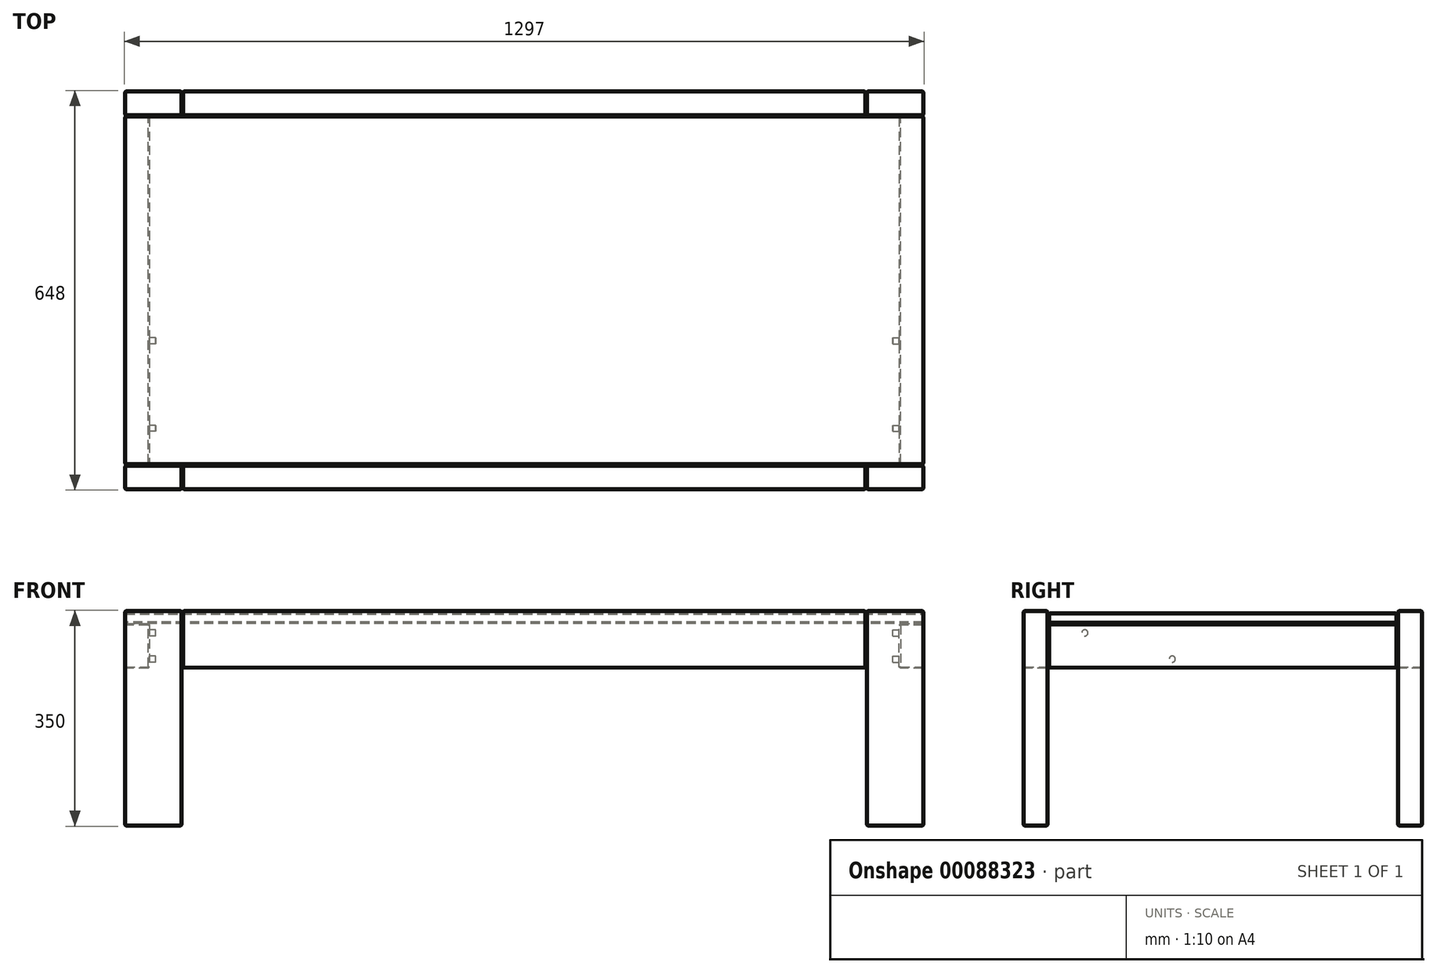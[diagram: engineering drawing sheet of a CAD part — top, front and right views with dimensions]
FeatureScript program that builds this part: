
annotation { "Feature Type Name" : "Feature", "Feature Type Description" : "" }
export const myFeature = defineFeature(function(context is Context, id is Id, definition is map)
    precondition{}
    {
        {
            var Q0;
            Q0=qCreatedBy(makeId("Top.planeOp"),FACE);
            var sketch = newSketch(context, id + "F0", { "sketchPlane" : qUnion([Q0])});
            skLineSegment(sketch, "E0.bottom", {"start": v(-648.5, 324) * mm, "end": v(648.5, 324) * mm, "construction": true});
            skLineSegment(sketch, "E0.top", {"start": v(-648.5, -324) * mm, "end": v(648.5, -324) * mm, "construction": true});
            skLineSegment(sketch, "E0.left", {"start": v(-648.5, 324) * mm, "end": v(-648.5, -324) * mm, "construction": true});
            skLineSegment(sketch, "E0.right", {"start": v(648.5, 324) * mm, "end": v(648.5, -324) * mm, "construction": true});
            skLineSegment(sketch, "E1", {"start": v(-648.5, -324) * mm, "end": v(648.5, 324) * mm, "construction": true});
            skLineSegment(sketch, "E2.bottom", {"start": v(-648.5, 324) * mm, "end": v(-554.5, 324) * mm});
            skLineSegment(sketch, "E2.top", {"start": v(-648.5, 283) * mm, "end": v(-554.5, 283) * mm});
            skLineSegment(sketch, "E2.left", {"start": v(-648.5, 324) * mm, "end": v(-648.5, 283) * mm});
            skLineSegment(sketch, "E2.right", {"start": v(-554.5, 324) * mm, "end": v(-554.5, 283) * mm});
            skLineSegment(sketch, "E3.bottom", {"start": v(-648.5, -324) * mm, "end": v(-554.5, -324) * mm});
            skLineSegment(sketch, "E3.top", {"start": v(-648.5, -283) * mm, "end": v(-554.5, -283) * mm});
            skLineSegment(sketch, "E3.left", {"start": v(-648.5, -324) * mm, "end": v(-648.5, -283) * mm});
            skLineSegment(sketch, "E3.right", {"start": v(-554.5, -324) * mm, "end": v(-554.5, -283) * mm});
            skLineSegment(sketch, "E4.bottom", {"start": v(648.5, 324) * mm, "end": v(554.5, 324) * mm});
            skLineSegment(sketch, "E4.top", {"start": v(648.5, 283) * mm, "end": v(554.5, 283) * mm});
            skLineSegment(sketch, "E4.left", {"start": v(648.5, 324) * mm, "end": v(648.5, 283) * mm});
            skLineSegment(sketch, "E4.right", {"start": v(554.5, 324) * mm, "end": v(554.5, 283) * mm});
            skLineSegment(sketch, "E5.bottom", {"start": v(648.5, -324) * mm, "end": v(554.5, -324) * mm});
            skLineSegment(sketch, "E5.top", {"start": v(648.5, -283) * mm, "end": v(554.5, -283) * mm});
            skLineSegment(sketch, "E5.left", {"start": v(648.5, -324) * mm, "end": v(648.5, -283) * mm});
            skLineSegment(sketch, "E5.right", {"start": v(554.5, -324) * mm, "end": v(554.5, -283) * mm});
            skSolve(sketch);
        }
        {
            var Q0;
            Q0 = qSketchRegion(id + "F0", true);
            extrude(context, id + "F1", {"entities" : qUnion([Q0]), "depth" : 350 * mm});
        }
        {
            var Q0;
            Q0=makeQuery(id+"F1.opExtrude","SWEPT_FACE",FACE,{"disambiguationData":[OSD([sQuery(id+"F0.wireOp",EDGE,"E3.right")])]});
            var sketch = newSketch(context, id + "F2", { "sketchPlane" : qUnion([Q0])});
            skLineSegment(sketch, "E6.bottom", {"start": v(-324, 350) * mm, "end": v(-283, 350) * mm});
            skLineSegment(sketch, "E6.top", {"start": v(-324, 256) * mm, "end": v(-283, 256) * mm});
            skLineSegment(sketch, "E6.left", {"start": v(-324, 350) * mm, "end": v(-324, 256) * mm});
            skLineSegment(sketch, "E6.right", {"start": v(-283, 350) * mm, "end": v(-283, 256) * mm});
            skLineSegment(sketch, "E7.bottom", {"start": v(283, 350) * mm, "end": v(324, 350) * mm});
            skLineSegment(sketch, "E7.top", {"start": v(283, 256) * mm, "end": v(324, 256) * mm});
            skLineSegment(sketch, "E7.left", {"start": v(283, 350) * mm, "end": v(283, 256) * mm});
            skLineSegment(sketch, "E7.right", {"start": v(324, 350) * mm, "end": v(324, 256) * mm});
            skSolve(sketch);
        }
        {
            var Q0;
            Q0 = qSketchRegion(id + "F2", true);
            var Q1;
            Q1=makeQuery(id+"F1.opExtrude","SWEPT_FACE",FACE,{"disambiguationData":[OSD([sQuery(id+"F0.wireOp",EDGE,"E5.right")])]});
            extrude(context, id + "F3", {"entities" : qUnion([Q0]), "endBound" : BoundingType.UP_TO_SURFACE, "endBoundEntityFace" : qUnion([Q1]), "depth" : 25 * mm});
        }
        {
            var Q0;
            Q0=makeQuery(id+"F3.opExtrude","SWEPT_FACE",FACE,{"disambiguationData":[OSD([sQuery(id+"F2.wireOp",EDGE,"E7.bottom")])]});
            cPlane(context, id + "F4", {"entities" : qUnion([Q0]), "cplaneType" : CPlaneType.OFFSET, "offset" : 3.5 * mm, "oppositeDirection" : true, "width" : 150 * mm, "height" : 150 * mm});
        }
        {
            var Q0;
            Q0=qCreatedBy(id+"F4.planeOp",FACE);
            var sketch = newSketch(context, id + "F5", { "sketchPlane" : qUnion([Q0])});
            skLineSegment(sketch, "E8.bottom", {"start": v(-648.5, 283) * mm, "end": v(648.5, 283) * mm});
            skLineSegment(sketch, "E8.top", {"start": v(-648.5, -283) * mm, "end": v(648.5, -283) * mm});
            skLineSegment(sketch, "E8.left", {"start": v(-648.5, 283) * mm, "end": v(-648.5, -283) * mm});
            skLineSegment(sketch, "E8.right", {"start": v(648.5, 283) * mm, "end": v(648.5, -283) * mm});
            skSolve(sketch);
        }
        {
            var Q0;
            Q0 = qSketchRegion(id + "F5", true);
            extrude(context, id + "F6", {"entities" : qUnion([Q0]), "oppositeDirection" : true, "depth" : 18 * mm});
        }
        {
            var Q0;
            Q0=makeQuery(id+"F1.opExtrude","SWEPT_FACE",FACE,{"disambiguationData":[OSD([sQuery(id+"F0.wireOp",EDGE,"E2.top")])]});
            var sketch = newSketch(context, id + "F7", { "sketchPlane" : qUnion([Q0])});
            skLineSegment(sketch, "E9", {"start": v(-648.5, 350) * mm, "end": v(-648.5, 256) * mm, "construction": true});
            skLineSegment(sketch, "E10.bottom", {"start": v(-648.5, 256) * mm, "end": v(-607.5, 256) * mm});
            skLineSegment(sketch, "E10.top", {"start": v(-648.5, 328.5) * mm, "end": v(-607.5, 328.5) * mm});
            skLineSegment(sketch, "E10.left", {"start": v(-648.5, 256) * mm, "end": v(-648.5, 328.5) * mm});
            skLineSegment(sketch, "E10.right", {"start": v(-607.5, 256) * mm, "end": v(-607.5, 328.5) * mm});
            skLineSegment(sketch, "E11", {"start": v(-607.5, 328.5) * mm, "end": v(-607.5, 350) * mm, "construction": true});
            skLineSegment(sketch, "E12.bottom", {"start": v(648.5, 328.5) * mm, "end": v(607.5, 328.5) * mm});
            skLineSegment(sketch, "E12.top", {"start": v(648.5, 256) * mm, "end": v(607.5, 256) * mm});
            skLineSegment(sketch, "E12.left", {"start": v(648.5, 328.5) * mm, "end": v(648.5, 256) * mm});
            skLineSegment(sketch, "E12.right", {"start": v(607.5, 328.5) * mm, "end": v(607.5, 256) * mm});
            skSolve(sketch);
        }
        {
            var Q0;
            Q0 = qSketchRegion(id + "F7", true);
            var Q1;
            Q1=makeQuery(id+"F1.opExtrude","SWEPT_FACE",FACE,{"disambiguationData":[OSD([sQuery(id+"F0.wireOp",EDGE,"E3.top")])]});
            extrude(context, id + "F8", {"entities" : qUnion([Q0]), "endBound" : BoundingType.UP_TO_SURFACE, "endBoundEntityFace" : qUnion([Q1]), "depth" : 25 * mm});
        }
        {
            var Q0;
            Q0=makeQuery(id+"F8.opExtrude","SWEPT_FACE",FACE,{"disambiguationData":[OSD([sQuery(id+"F7.wireOp",EDGE,"E10.right")])]});
            var sketch = newSketch(context, id + "F9", { "sketchPlane" : qUnion([Q0])});
            skPoint(sketch, "E13", {"position": v(-82, 271) * mm});
            skPoint(sketch, "E14", {"position": v(-223.7, 313.5) * mm});
            skLineSegment(sketch, "E15", {"start": v(-223.7, 313.5) * mm, "end": v(-230.84, 300.3) * mm, "construction": true});
            skLineSegment(sketch, "E16", {"start": v(-230.84, 300.3) * mm, "end": v(-283, 328.5) * mm, "construction": true});
            skLineSegment(sketch, "E17", {"start": v(-223.7, 313.5) * mm, "end": v(-531.6, 479.94) * mm, "construction": true});
            skLineSegment(sketch, "E18", {"start": v(-389.9, 437.44) * mm, "end": v(-82, 271) * mm, "construction": true});
            skLineSegment(sketch, "E19", {"start": v(-389.9, 437.44) * mm, "end": v(-531.6, 479.94) * mm, "construction": true});
            skLineSegment(sketch, "E20", {"start": v(-82, 271) * mm, "end": v(268, 271) * mm, "construction": true});
            skCircle(sketch, "E21", {"center": v(-223.7, 313.5) * mm, "radius": 5 * mm});
            skCircle(sketch, "E22", {"center": v(-82, 271) * mm, "radius": 5 * mm});
            skSolve(sketch);
        }
        {
            var Q0;
            Q0=makeQuery(id+"F3.opExtrude","CAP_EDGE",EDGE,{"disambiguationData":[OSD([sQuery(id+"F2.wireOp",EDGE,"E7.right")])],"isStart":true});
            var Q1;
            Q1=makeQuery(id+"F3.opExtrude","CAP_EDGE",EDGE,{"disambiguationData":[OSD([sQuery(id+"F2.wireOp",EDGE,"E7.left")])],"isStart":false});
            var Q2;
            Q2=makeQuery(id+"F3.opExtrude","CAP_EDGE",EDGE,{"disambiguationData":[OSD([sQuery(id+"F2.wireOp",EDGE,"E7.left")])],"isStart":true});
            var Q3;
            Q3=makeQuery(id+"F3.opExtrude","CAP_EDGE",EDGE,{"disambiguationData":[OSD([sQuery(id+"F2.wireOp",EDGE,"E7.top")])],"isStart":false});
            var Q4;
            Q4=makeQuery(id+"F1.opExtrude","CAP_EDGE",EDGE,{"disambiguationData":[OSD([sQuery(id+"F0.wireOp",EDGE,"E2.right")])],"isStart":false});
            var Q5;
            Q5=makeQuery(id+"F1.opExtrude","CAP_EDGE",EDGE,{"disambiguationData":[OSD([sQuery(id+"F0.wireOp",EDGE,"E3.right")])],"isStart":false});
            var Q6;
            Q6=makeQuery(id+"F1.opExtrude","CAP_EDGE",EDGE,{"disambiguationData":[OSD([sQuery(id+"F0.wireOp",EDGE,"E4.right")])],"isStart":false});
            var Q7;
            Q7=makeQuery(id+"F1.opExtrude","CAP_EDGE",EDGE,{"disambiguationData":[OSD([sQuery(id+"F0.wireOp",EDGE,"E5.right")])],"isStart":false});
            var Q8;
            Q8=makeQuery(id+"F1.opExtrude","CAP_EDGE",EDGE,{"disambiguationData":[OSD([sQuery(id+"F0.wireOp",EDGE,"E5.bottom")])],"isStart":true});
            var Q9;
            Q9=makeQuery(id+"F1.opExtrude","CAP_EDGE",EDGE,{"disambiguationData":[OSD([sQuery(id+"F0.wireOp",EDGE,"E5.top")])],"isStart":false});
            var Q10;
            Q10=makeQuery(id+"F1.opExtrude","CAP_EDGE",EDGE,{"disambiguationData":[OSD([sQuery(id+"F0.wireOp",EDGE,"E5.top")])],"isStart":true});
            var Q11;
            Q11=makeQuery(id+"F3.opExtrude","CAP_EDGE",EDGE,{"disambiguationData":[OSD([sQuery(id+"F2.wireOp",EDGE,"E7.right")])],"isStart":false});
            var Q12;
            Q12=makeQuery(id+"F3.opExtrude","CAP_EDGE",EDGE,{"disambiguationData":[OSD([sQuery(id+"F2.wireOp",EDGE,"E6.bottom")])],"isStart":false});
            var Q13;
            Q13=makeQuery(id+"F3.opExtrude","CAP_EDGE",EDGE,{"disambiguationData":[OSD([sQuery(id+"F2.wireOp",EDGE,"E7.bottom")])],"isStart":true});
            var Q14;
            Q14=makeQuery(id+"F3.opExtrude","CAP_EDGE",EDGE,{"disambiguationData":[OSD([sQuery(id+"F2.wireOp",EDGE,"E7.bottom")])],"isStart":false});
            var Q15;
            Q15=makeQuery(id+"F3.opExtrude","SWEPT_EDGE",EDGE,{"disambiguationData":[OSD([sQuery(id+"F2.wireOp",EDGE,"E7.bottom"),sQuery(id+"F2.wireOp",EDGE,"E7.right")])]});
            var Q16;
            Q16=makeQuery(id+"F1.opExtrude","SWEPT_EDGE",EDGE,{"disambiguationData":[OSD([sQuery(id+"F0.wireOp",EDGE,"E2.top"),sQuery(id+"F0.wireOp",EDGE,"E2.right")])]});
            var Q17;
            Q17=makeQuery(id+"F1.opExtrude","SWEPT_EDGE",EDGE,{"disambiguationData":[OSD([sQuery(id+"F0.wireOp",EDGE,"E2.bottom"),sQuery(id+"F0.wireOp",EDGE,"E2.right")])]});
            var Q18;
            Q18=makeQuery(id+"F1.opExtrude","SWEPT_EDGE",EDGE,{"disambiguationData":[OSD([sQuery(id+"F0.wireOp",EDGE,"E2.top"),sQuery(id+"F0.wireOp",EDGE,"E2.left")])]});
            var Q19;
            Q19=makeQuery(id+"F1.opExtrude","CAP_EDGE",EDGE,{"disambiguationData":[OSD([sQuery(id+"F0.wireOp",EDGE,"E2.top")])],"isStart":false});
            var Q20;
            Q20=makeQuery(id+"F8.opExtrude","CAP_EDGE",EDGE,{"disambiguationData":[OSD([sQuery(id+"F7.wireOp",EDGE,"E12.bottom")])],"isStart":true});
            var Q21;
            Q21=makeQuery(id+"F8.opExtrude","SWEPT_EDGE",EDGE,{"disambiguationData":[OSD([sQuery(id+"F7.wireOp",EDGE,"E12.bottom"),sQuery(id+"F7.wireOp",EDGE,"E12.left")])]});
            var Q22;
            Q22=makeQuery(id+"F8.opExtrude","SWEPT_EDGE",EDGE,{"disambiguationData":[OSD([sQuery(id+"F7.wireOp",EDGE,"E12.top"),sQuery(id+"F7.wireOp",EDGE,"E12.left")])]});
            var Q23;
            Q23=makeQuery(id+"F8.opExtrude","SWEPT_EDGE",EDGE,{"disambiguationData":[OSD([sQuery(id+"F7.wireOp",EDGE,"E12.bottom"),sQuery(id+"F7.wireOp",EDGE,"E12.right")])]});
            var Q24;
            Q24=makeQuery(id+"F1.opExtrude","SWEPT_EDGE",EDGE,{"disambiguationData":[OSD([sQuery(id+"F0.wireOp",EDGE,"E3.bottom"),sQuery(id+"F0.wireOp",EDGE,"E3.right")])]});
            var Q25;
            Q25=makeQuery(id+"F1.opExtrude","SWEPT_EDGE",EDGE,{"disambiguationData":[OSD([sQuery(id+"F0.wireOp",EDGE,"E3.top"),sQuery(id+"F0.wireOp",EDGE,"E3.right")])]});
            var Q26;
            Q26=makeQuery(id+"F1.opExtrude","SWEPT_EDGE",EDGE,{"disambiguationData":[OSD([sQuery(id+"F0.wireOp",EDGE,"E3.bottom"),sQuery(id+"F0.wireOp",EDGE,"E3.left")])]});
            var Q27;
            Q27=makeQuery(id+"F1.opExtrude","SWEPT_EDGE",EDGE,{"disambiguationData":[OSD([sQuery(id+"F0.wireOp",EDGE,"E5.bottom"),sQuery(id+"F0.wireOp",EDGE,"E5.left")])]});
            var Q28;
            Q28=makeQuery(id+"F1.opExtrude","SWEPT_EDGE",EDGE,{"disambiguationData":[OSD([sQuery(id+"F0.wireOp",EDGE,"E5.top"),sQuery(id+"F0.wireOp",EDGE,"E5.left")])]});
            var Q29;
            Q29=makeQuery(id+"F1.opExtrude","SWEPT_EDGE",EDGE,{"disambiguationData":[OSD([sQuery(id+"F0.wireOp",EDGE,"E5.bottom"),sQuery(id+"F0.wireOp",EDGE,"E5.right")])]});
            var Q30;
            Q30=makeQuery(id+"F1.opExtrude","CAP_EDGE",EDGE,{"disambiguationData":[OSD([sQuery(id+"F0.wireOp",EDGE,"E5.left")])],"isStart":true});
            var Q31;
            Q31=makeQuery(id+"F1.opExtrude","SWEPT_EDGE",EDGE,{"disambiguationData":[OSD([sQuery(id+"F0.wireOp",EDGE,"E4.top"),sQuery(id+"F0.wireOp",EDGE,"E4.right")])]});
            var Q32;
            Q32=makeQuery(id+"F1.opExtrude","SWEPT_EDGE",EDGE,{"disambiguationData":[OSD([sQuery(id+"F0.wireOp",EDGE,"E4.top"),sQuery(id+"F0.wireOp",EDGE,"E4.left")])]});
            var Q33;
            Q33=makeQuery(id+"F1.opExtrude","SWEPT_EDGE",EDGE,{"disambiguationData":[OSD([sQuery(id+"F0.wireOp",EDGE,"E4.bottom"),sQuery(id+"F0.wireOp",EDGE,"E4.left")])]});
            var Q34;
            Q34=makeQuery(id+"F1.opExtrude","CAP_EDGE",EDGE,{"disambiguationData":[OSD([sQuery(id+"F0.wireOp",EDGE,"E4.left")])],"isStart":false});
            var Q35;
            Q35=makeQuery(id+"F8.opExtrude","SWEPT_EDGE",EDGE,{"disambiguationData":[OSD([sQuery(id+"F0.wireOp",EDGE,"E2.top"),sQuery(id+"F0.wireOp",EDGE,"E2.left"),sQuery(id+"F7.wireOp",EDGE,"E10.top"),sQuery(id+"F7.wireOp",EDGE,"E10.left")])]});
            var Q36;
            Q36=makeQuery(id+"F8.opExtrude","SWEPT_EDGE",EDGE,{"disambiguationData":[OSD([sQuery(id+"F7.wireOp",EDGE,"E10.bottom"),sQuery(id+"F7.wireOp",EDGE,"E10.right")])]});
            var Q37;
            Q37=makeQuery(id+"F8.opExtrude","SWEPT_EDGE",EDGE,{"disambiguationData":[OSD([sQuery(id+"F7.wireOp",EDGE,"E10.top"),sQuery(id+"F7.wireOp",EDGE,"E10.right")])]});
            var Q38;
            Q38=makeQuery(id+"F3.opExtrude","SWEPT_EDGE",EDGE,{"disambiguationData":[OSD([sQuery(id+"F2.wireOp",EDGE,"E6.bottom"),sQuery(id+"F2.wireOp",EDGE,"E6.right")])]});
            var Q39;
            Q39=makeQuery(id+"F3.opExtrude","SWEPT_EDGE",EDGE,{"disambiguationData":[OSD([sQuery(id+"F2.wireOp",EDGE,"E7.top"),sQuery(id+"F2.wireOp",EDGE,"E7.left")])]});
            var Q40;
            Q40=makeQuery(id+"F3.opExtrude","SWEPT_EDGE",EDGE,{"disambiguationData":[OSD([sQuery(id+"F2.wireOp",EDGE,"E7.top"),sQuery(id+"F2.wireOp",EDGE,"E7.right")])]});
            var Q41;
            Q41=makeQuery(id+"F3.opExtrude","SWEPT_EDGE",EDGE,{"disambiguationData":[OSD([sQuery(id+"F2.wireOp",EDGE,"E7.bottom"),sQuery(id+"F2.wireOp",EDGE,"E7.left")])]});
            var Q42;
            Q42=makeQuery(id+"F3.opExtrude","CAP_EDGE",EDGE,{"disambiguationData":[OSD([sQuery(id+"F2.wireOp",EDGE,"E7.top")])],"isStart":true});
            var Q43;
            Q43=makeQuery(id+"F1.opExtrude","CAP_EDGE",EDGE,{"disambiguationData":[OSD([sQuery(id+"F0.wireOp",EDGE,"E2.bottom")])],"isStart":false});
            var Q44;
            Q44=makeQuery(id+"F1.opExtrude","CAP_EDGE",EDGE,{"disambiguationData":[OSD([sQuery(id+"F0.wireOp",EDGE,"E2.left")])],"isStart":false});
            var Q45;
            Q45=makeQuery(id+"F1.opExtrude","CAP_EDGE",EDGE,{"disambiguationData":[OSD([sQuery(id+"F0.wireOp",EDGE,"E2.left")])],"isStart":true});
            var Q46;
            Q46=makeQuery(id+"F1.opExtrude","CAP_EDGE",EDGE,{"disambiguationData":[OSD([sQuery(id+"F0.wireOp",EDGE,"E2.right")])],"isStart":true});
            var Q47;
            Q47=makeQuery(id+"F1.opExtrude","SWEPT_EDGE",EDGE,{"disambiguationData":[OSD([sQuery(id+"F0.wireOp",EDGE,"E2.bottom"),sQuery(id+"F0.wireOp",EDGE,"E2.left")])]});
            var Q48;
            Q48=makeQuery(id+"F8.opExtrude","CAP_EDGE",EDGE,{"disambiguationData":[OSD([sQuery(id+"F7.wireOp",EDGE,"E12.top")])],"isStart":true});
            var Q49;
            Q49=makeQuery(id+"F8.opExtrude","CAP_EDGE",EDGE,{"disambiguationData":[OSD([sQuery(id+"F7.wireOp",EDGE,"E12.bottom")])],"isStart":false});
            var Q50;
            Q50=makeQuery(id+"F8.opExtrude","CAP_EDGE",EDGE,{"disambiguationData":[OSD([sQuery(id+"F7.wireOp",EDGE,"E12.top")])],"isStart":false});
            var Q51;
            Q51=makeQuery(id+"F8.opExtrude","CAP_EDGE",EDGE,{"disambiguationData":[OSD([sQuery(id+"F7.wireOp",EDGE,"E12.left")])],"isStart":true});
            var Q52;
            Q52=makeQuery(id+"F8.opExtrude","CAP_EDGE",EDGE,{"disambiguationData":[OSD([sQuery(id+"F7.wireOp",EDGE,"E12.left")])],"isStart":false});
            var Q53;
            Q53=makeQuery(id+"F8.opExtrude","CAP_EDGE",EDGE,{"disambiguationData":[OSD([sQuery(id+"F7.wireOp",EDGE,"E12.right")])],"isStart":true});
            var Q54;
            Q54=makeQuery(id+"F8.opExtrude","CAP_EDGE",EDGE,{"disambiguationData":[OSD([sQuery(id+"F7.wireOp",EDGE,"E12.right")])],"isStart":false});
            var Q55;
            Q55=makeQuery(id+"F8.opExtrude","SWEPT_EDGE",EDGE,{"disambiguationData":[OSD([sQuery(id+"F7.wireOp",EDGE,"E12.top"),sQuery(id+"F7.wireOp",EDGE,"E12.right")])]});
            var Q56;
            Q56=makeQuery(id+"F1.opExtrude","CAP_EDGE",EDGE,{"disambiguationData":[OSD([sQuery(id+"F0.wireOp",EDGE,"E3.top")])],"isStart":false});
            var Q57;
            Q57=makeQuery(id+"F1.opExtrude","SWEPT_EDGE",EDGE,{"disambiguationData":[OSD([sQuery(id+"F0.wireOp",EDGE,"E3.top"),sQuery(id+"F0.wireOp",EDGE,"E3.left")])]});
            var Q58;
            Q58=makeQuery(id+"F1.opExtrude","CAP_EDGE",EDGE,{"disambiguationData":[OSD([sQuery(id+"F0.wireOp",EDGE,"E3.bottom")])],"isStart":true});
            var Q59;
            Q59=makeQuery(id+"F1.opExtrude","CAP_EDGE",EDGE,{"disambiguationData":[OSD([sQuery(id+"F0.wireOp",EDGE,"E3.bottom")])],"isStart":false});
            var Q60;
            Q60=makeQuery(id+"F1.opExtrude","CAP_EDGE",EDGE,{"disambiguationData":[OSD([sQuery(id+"F0.wireOp",EDGE,"E3.top")])],"isStart":true});
            var Q61;
            Q61=makeQuery(id+"F1.opExtrude","CAP_EDGE",EDGE,{"disambiguationData":[OSD([sQuery(id+"F0.wireOp",EDGE,"E3.right")])],"isStart":true});
            var Q62;
            Q62=makeQuery(id+"F1.opExtrude","CAP_EDGE",EDGE,{"disambiguationData":[OSD([sQuery(id+"F0.wireOp",EDGE,"E3.left")])],"isStart":true});
            var Q63;
            Q63=makeQuery(id+"F1.opExtrude","CAP_EDGE",EDGE,{"disambiguationData":[OSD([sQuery(id+"F0.wireOp",EDGE,"E3.left")])],"isStart":false});
            var Q64;
            Q64=makeQuery(id+"F1.opExtrude","CAP_EDGE",EDGE,{"disambiguationData":[OSD([sQuery(id+"F0.wireOp",EDGE,"E5.bottom")])],"isStart":false});
            var Q65;
            Q65=makeQuery(id+"F1.opExtrude","SWEPT_EDGE",EDGE,{"disambiguationData":[OSD([sQuery(id+"F0.wireOp",EDGE,"E5.top"),sQuery(id+"F0.wireOp",EDGE,"E5.right")])]});
            var Q66;
            Q66=makeQuery(id+"F1.opExtrude","CAP_EDGE",EDGE,{"disambiguationData":[OSD([sQuery(id+"F0.wireOp",EDGE,"E5.right")])],"isStart":true});
            var Q67;
            Q67=makeQuery(id+"F1.opExtrude","CAP_EDGE",EDGE,{"disambiguationData":[OSD([sQuery(id+"F0.wireOp",EDGE,"E5.left")])],"isStart":false});
            var Q68;
            Q68=makeQuery(id+"F1.opExtrude","CAP_EDGE",EDGE,{"disambiguationData":[OSD([sQuery(id+"F0.wireOp",EDGE,"E4.top")])],"isStart":false});
            var Q69;
            Q69=makeQuery(id+"F1.opExtrude","CAP_EDGE",EDGE,{"disambiguationData":[OSD([sQuery(id+"F0.wireOp",EDGE,"E4.bottom")])],"isStart":false});
            var Q70;
            Q70=makeQuery(id+"F1.opExtrude","SWEPT_EDGE",EDGE,{"disambiguationData":[OSD([sQuery(id+"F0.wireOp",EDGE,"E4.bottom"),sQuery(id+"F0.wireOp",EDGE,"E4.right")])]});
            var Q71;
            Q71=makeQuery(id+"F1.opExtrude","CAP_EDGE",EDGE,{"disambiguationData":[OSD([sQuery(id+"F0.wireOp",EDGE,"E4.left")])],"isStart":true});
            var Q72;
            Q72=makeQuery(id+"F1.opExtrude","CAP_EDGE",EDGE,{"disambiguationData":[OSD([sQuery(id+"F0.wireOp",EDGE,"E4.right")])],"isStart":true});
            var Q73;
            Q73=makeQuery(id+"F1.opExtrude","CAP_EDGE",EDGE,{"disambiguationData":[OSD([sQuery(id+"F0.wireOp",EDGE,"E4.bottom")])],"isStart":true});
            var Q74;
            Q74=makeQuery(id+"F1.opExtrude","CAP_EDGE",EDGE,{"disambiguationData":[OSD([sQuery(id+"F0.wireOp",EDGE,"E4.top")])],"isStart":true});
            var Q75;
            Q75=makeQuery(id+"F8.opExtrude","CAP_EDGE",EDGE,{"disambiguationData":[OSD([sQuery(id+"F7.wireOp",EDGE,"E10.top")])],"isStart":true});
            var Q76;
            Q76=makeQuery(id+"F8.opExtrude","CAP_EDGE",EDGE,{"disambiguationData":[OSD([sQuery(id+"F7.wireOp",EDGE,"E10.left")])],"isStart":true});
            var Q77;
            Q77=makeQuery(id+"F8.opExtrude","SWEPT_EDGE",EDGE,{"disambiguationData":[OSD([sQuery(id+"F0.wireOp",EDGE,"E2.top"),sQuery(id+"F0.wireOp",EDGE,"E2.left"),sQuery(id+"F7.wireOp",EDGE,"E10.bottom"),sQuery(id+"F7.wireOp",EDGE,"E10.left")])]});
            var Q78;
            Q78=makeQuery(id+"F8.opExtrude","CAP_EDGE",EDGE,{"disambiguationData":[OSD([sQuery(id+"F7.wireOp",EDGE,"E10.bottom")])],"isStart":true});
            var Q79;
            Q79=makeQuery(id+"F8.opExtrude","CAP_EDGE",EDGE,{"disambiguationData":[OSD([sQuery(id+"F7.wireOp",EDGE,"E10.left")])],"isStart":false});
            var Q80;
            Q80=makeQuery(id+"F8.opExtrude","CAP_EDGE",EDGE,{"disambiguationData":[OSD([sQuery(id+"F7.wireOp",EDGE,"E10.right")])],"isStart":true});
            var Q81;
            Q81=makeQuery(id+"F8.opExtrude","CAP_EDGE",EDGE,{"disambiguationData":[OSD([sQuery(id+"F7.wireOp",EDGE,"E10.right")])],"isStart":false});
            var Q82;
            Q82=makeQuery(id+"F3.opExtrude","CAP_EDGE",EDGE,{"disambiguationData":[OSD([sQuery(id+"F2.wireOp",EDGE,"E6.top")])],"isStart":true});
            var Q83;
            Q83=makeQuery(id+"F3.opExtrude","CAP_EDGE",EDGE,{"disambiguationData":[OSD([sQuery(id+"F2.wireOp",EDGE,"E6.left")])],"isStart":true});
            var Q84;
            Q84=makeQuery(id+"F3.opExtrude","SWEPT_EDGE",EDGE,{"disambiguationData":[OSD([sQuery(id+"F0.wireOp",EDGE,"E3.top"),sQuery(id+"F0.wireOp",EDGE,"E3.right"),sQuery(id+"F2.wireOp",EDGE,"E6.top"),sQuery(id+"F2.wireOp",EDGE,"E6.right")])]});
            var Q85;
            Q85=makeQuery(id+"F3.opExtrude","SWEPT_EDGE",EDGE,{"disambiguationData":[OSD([sQuery(id+"F0.wireOp",EDGE,"E3.bottom"),sQuery(id+"F0.wireOp",EDGE,"E3.right"),sQuery(id+"F2.wireOp",EDGE,"E6.top"),sQuery(id+"F2.wireOp",EDGE,"E6.left")])]});
            var Q86;
            Q86=makeQuery(id+"F3.opExtrude","CAP_EDGE",EDGE,{"disambiguationData":[OSD([sQuery(id+"F2.wireOp",EDGE,"E6.left")])],"isStart":false});
            var Q87;
            Q87=makeQuery(id+"F3.opExtrude","CAP_EDGE",EDGE,{"disambiguationData":[OSD([sQuery(id+"F2.wireOp",EDGE,"E6.right")])],"isStart":true});
            var Q88;
            Q88=makeQuery(id+"F3.opExtrude","CAP_EDGE",EDGE,{"disambiguationData":[OSD([sQuery(id+"F2.wireOp",EDGE,"E6.right")])],"isStart":false});
            var Q89;
            Q89=makeQuery(id+"F3.opExtrude","SWEPT_EDGE",EDGE,{"disambiguationData":[OSD([sQuery(id+"F2.wireOp",EDGE,"E6.bottom"),sQuery(id+"F2.wireOp",EDGE,"E6.left")])]});
            var Q90;
            Q90=makeQuery(id+"F1.opExtrude","CAP_EDGE",EDGE,{"disambiguationData":[OSD([sQuery(id+"F0.wireOp",EDGE,"E2.top")])],"isStart":true});
            var Q91;
            Q91=makeQuery(id+"F1.opExtrude","CAP_EDGE",EDGE,{"disambiguationData":[OSD([sQuery(id+"F0.wireOp",EDGE,"E2.bottom")])],"isStart":true});
            var Q92;
            Q92=makeQuery(id+"F8.opExtrude","CAP_EDGE",EDGE,{"disambiguationData":[OSD([sQuery(id+"F7.wireOp",EDGE,"E10.bottom")])],"isStart":false});
            var Q93;
            Q93=makeQuery(id+"F8.opExtrude","CAP_EDGE",EDGE,{"disambiguationData":[OSD([sQuery(id+"F7.wireOp",EDGE,"E10.top")])],"isStart":false});
            var Q94;
            Q94=makeQuery(id+"F3.opExtrude","CAP_EDGE",EDGE,{"disambiguationData":[OSD([sQuery(id+"F2.wireOp",EDGE,"E6.bottom")])],"isStart":true});
            var Q95;
            Q95=makeQuery(id+"F3.opExtrude","CAP_EDGE",EDGE,{"disambiguationData":[OSD([sQuery(id+"F2.wireOp",EDGE,"E6.top")])],"isStart":false});
            var Q96;
            Q96=makeQuery(id+"F6.opExtrude","CAP_EDGE",EDGE,{"disambiguationData":[OSD([sQuery(id+"F5.wireOp",EDGE,"E8.bottom")])],"isStart":true});
            var Q97;
            Q97=makeQuery(id+"F6.opExtrude","CAP_EDGE",EDGE,{"disambiguationData":[OSD([sQuery(id+"F5.wireOp",EDGE,"E8.left")])],"isStart":true});
            var Q98;
            Q98=makeQuery(id+"F6.opExtrude","CAP_EDGE",EDGE,{"disambiguationData":[OSD([sQuery(id+"F5.wireOp",EDGE,"E8.right")])],"isStart":true});
            var Q99;
            Q99=makeQuery(id+"F6.opExtrude","CAP_EDGE",EDGE,{"disambiguationData":[OSD([sQuery(id+"F5.wireOp",EDGE,"E8.right")])],"isStart":false});
            var Q100;
            Q100=makeQuery(id+"F6.opExtrude","SWEPT_EDGE",EDGE,{"disambiguationData":[OSD([sQuery(id+"F5.wireOp",EDGE,"E8.bottom"),sQuery(id+"F5.wireOp",EDGE,"E8.right")])]});
            var Q101;
            Q101=makeQuery(id+"F6.opExtrude","CAP_EDGE",EDGE,{"disambiguationData":[OSD([sQuery(id+"F5.wireOp",EDGE,"E8.bottom")])],"isStart":false});
            var Q102;
            Q102=makeQuery(id+"F6.opExtrude","CAP_EDGE",EDGE,{"disambiguationData":[OSD([sQuery(id+"F5.wireOp",EDGE,"E8.top")])],"isStart":true});
            var Q103;
            Q103=makeQuery(id+"F6.opExtrude","CAP_EDGE",EDGE,{"disambiguationData":[OSD([sQuery(id+"F5.wireOp",EDGE,"E8.top")])],"isStart":false});
            var Q104;
            Q104=makeQuery(id+"F6.opExtrude","CAP_EDGE",EDGE,{"disambiguationData":[OSD([sQuery(id+"F5.wireOp",EDGE,"E8.left")])],"isStart":false});
            var Q105;
            Q105=makeQuery(id+"F6.opExtrude","SWEPT_EDGE",EDGE,{"disambiguationData":[OSD([sQuery(id+"F5.wireOp",EDGE,"E8.bottom"),sQuery(id+"F5.wireOp",EDGE,"E8.left")])]});
            var Q106;
            Q106=makeQuery(id+"F6.opExtrude","SWEPT_EDGE",EDGE,{"disambiguationData":[OSD([sQuery(id+"F5.wireOp",EDGE,"E8.top"),sQuery(id+"F5.wireOp",EDGE,"E8.left")])]});
            var Q107;
            Q107=makeQuery(id+"F6.opExtrude","SWEPT_EDGE",EDGE,{"disambiguationData":[OSD([sQuery(id+"F5.wireOp",EDGE,"E8.top"),sQuery(id+"F5.wireOp",EDGE,"E8.right")])]});
            chamfer(context, id + "F10", {"entities" : qUnion([Q0, Q1, Q2, Q3, Q4, Q5, Q6, Q7, Q8, Q9, Q10, Q11, Q12, Q13, Q14, Q15, Q16, Q17, Q18, Q19, Q20, Q21, Q22, Q23, Q24, Q25, Q26, Q27, Q28, Q29, Q30, Q31, Q32, Q33, Q34, Q35, Q36, Q37, Q38, Q39, Q40, Q41, Q42, Q43, Q44, Q45, Q46, Q47, Q48, Q49, Q50, Q51, Q52, Q53, Q54, Q55, Q56, Q57, Q58, Q59, Q60, Q61, Q62, Q63, Q64, Q65, Q66, Q67, Q68, Q69, Q70, Q71, Q72, Q73, Q74, Q75, Q76, Q77, Q78, Q79, Q80, Q81, Q82, Q83, Q84, Q85, Q86, Q87, Q88, Q89, Q90, Q91, Q92, Q93, Q94, Q95, Q96, Q97, Q98, Q99, Q100, Q101, Q102, Q103, Q104, Q105, Q106, Q107]), "width" : 2.5 * mm, "tangentPropagation" : true});
        }
        {
            var Q0;
            Q0 = qSketchRegion(id + "F9", true);
            extrude(context, id + "F11", {"entities" : qUnion([Q0]), "depth" : 10 * mm});
        }
        {
            var Q0;
            Q0=makeQuery(id+"F11.opExtrude","SWEPT_BODY",BODY,{"disambiguationData":[OSD([sQuery(id+"F9.wireOp",EDGE,"E21")])]});
            var Q1;
            Q1=makeQuery(id+"F11.opExtrude","SWEPT_BODY",BODY,{"disambiguationData":[OSD([sQuery(id+"F9.wireOp",EDGE,"E22")])]});
            var Q2;
            Q2=qCreatedBy(makeId("Right.planeOp"),FACE);
            mirror(context, id + "F12", {"entities" : qUnion([Q0, Q1]), "mirrorPlane" : qUnion([Q2])});
        }
    });
